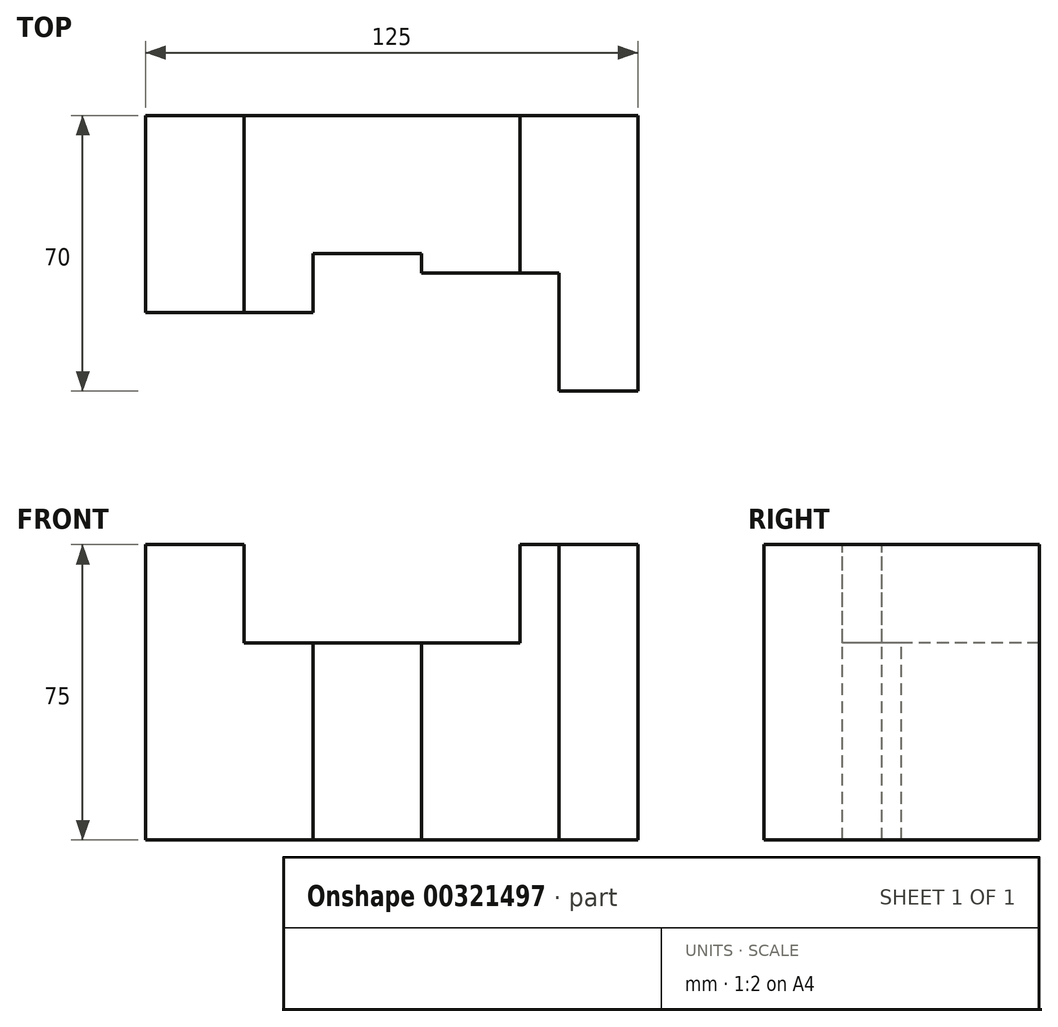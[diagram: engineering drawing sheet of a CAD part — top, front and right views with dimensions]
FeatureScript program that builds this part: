
annotation { "Feature Type Name" : "Feature", "Feature Type Description" : "" }
export const myFeature = defineFeature(function(context is Context, id is Id, definition is map)
    precondition{}
    {
        {
            var Q0;
            Q0=qCreatedBy(makeId("Right.planeOp"),FACE);
            var sketch = newSketch(context, id + "F0", { "sketchPlane" : qUnion([Q0])});
            skLineSegment(sketch, "E0.bottom", {"start": v(0, 0) * mm, "end": v(-50, 0) * mm});
            skLineSegment(sketch, "E0.top", {"start": v(0, 75) * mm, "end": v(-50, 75) * mm});
            skLineSegment(sketch, "E0.left", {"start": v(0, 0) * mm, "end": v(0, 75) * mm});
            skLineSegment(sketch, "E0.right", {"start": v(-50, 0) * mm, "end": v(-50, 75) * mm});
            skSolve(sketch);
        }
        {
            var Q0;
            Q0 = qSketchRegion(id + "F0", true);
            extrude(context, id + "F1", {"entities" : qUnion([Q0]), "depth" : 25 * mm});
        }
        {
            var Q0;
            Q0=makeQuery(id+"F1.opExtrude","CAP_FACE",FACE,{"disambiguationData":[OSD([sQuery(id+"F0.wireOp",EDGE,"E0.bottom"),sQuery(id+"F0.wireOp",EDGE,"E0.top"),sQuery(id+"F0.wireOp",EDGE,"E0.left"),sQuery(id+"F0.wireOp",EDGE,"E0.right")])],"isStart":false});
            var sketch = newSketch(context, id + "F2", { "sketchPlane" : qUnion([Q0])});
            skLineSegment(sketch, "E1.bottom", {"start": v(0, 0) * mm, "end": v(-50, 0) * mm});
            skLineSegment(sketch, "E1.top", {"start": v(0, 50) * mm, "end": v(-50, 50) * mm});
            skLineSegment(sketch, "E1.left", {"start": v(0, 0) * mm, "end": v(0, 50) * mm});
            skLineSegment(sketch, "E1.right", {"start": v(-50, 0) * mm, "end": v(-50, 50) * mm});
            skSolve(sketch);
        }
        {
            var Q0;
            Q0=makeQuery(id+"F2.imprint","IMPRINT",FACE,{"disambiguationData":[TD([[makeQuery(id+"F2.imprint","IMPRINT",EDGE,{"derivedFrom":sQuery(id+"F2.wireOp",EDGE,"E1.bottom")}),-1.0]])]});
            extrude(context, id + "F3", {"entities" : qUnion([Q0]), "operationType" : NewBodyOperationType.ADD, "depth" : 17.5 * mm});
        }
        {
            var Q0;
            Q0=makeQuery(id+"F3.opExtrude","CAP_FACE",FACE,{"disambiguationData":[OSD([sQuery(id+"F2.wireOp",EDGE,"E1.bottom"),sQuery(id+"F2.wireOp",EDGE,"E1.top"),sQuery(id+"F2.wireOp",EDGE,"E1.left"),sQuery(id+"F2.wireOp",EDGE,"E1.right")])],"isStart":false});
            var sketch = newSketch(context, id + "F4", { "sketchPlane" : qUnion([Q0])});
            skLineSegment(sketch, "E2.bottom", {"start": v(0, 0) * mm, "end": v(-35, 0) * mm});
            skLineSegment(sketch, "E2.top", {"start": v(0, 50) * mm, "end": v(-35, 50) * mm});
            skLineSegment(sketch, "E2.left", {"start": v(0, 0) * mm, "end": v(0, 50) * mm});
            skLineSegment(sketch, "E2.right", {"start": v(-35, 0) * mm, "end": v(-35, 50) * mm});
            skSolve(sketch);
        }
        {
            var Q0;
            Q0 = qSketchRegion(id + "F4", true);
            extrude(context, id + "F5", {"entities" : qUnion([Q0]), "operationType" : NewBodyOperationType.ADD, "depth" : 27.5 * mm});
        }
        {
            var Q0;
            Q0=makeQuery(id+"F5.opExtrude","CAP_FACE",FACE,{"disambiguationData":[OSD([sQuery(id+"F4.wireOp",EDGE,"E2.bottom"),sQuery(id+"F4.wireOp",EDGE,"E2.top"),sQuery(id+"F4.wireOp",EDGE,"E2.left"),sQuery(id+"F4.wireOp",EDGE,"E2.right")])],"isStart":false});
            var sketch = newSketch(context, id + "F6", { "sketchPlane" : qUnion([Q0])});
            skLineSegment(sketch, "E3.bottom", {"start": v(0, 0) * mm, "end": v(-40, 0) * mm});
            skLineSegment(sketch, "E3.top", {"start": v(0, 50) * mm, "end": v(-40, 50) * mm});
            skLineSegment(sketch, "E3.left", {"start": v(0, 0) * mm, "end": v(0, 50) * mm});
            skLineSegment(sketch, "E3.right", {"start": v(-40, 0) * mm, "end": v(-40, 50) * mm});
            skSolve(sketch);
        }
        {
            var Q0;
            Q0 = qSketchRegion(id + "F6", true);
            extrude(context, id + "F7", {"entities" : qUnion([Q0]), "operationType" : NewBodyOperationType.ADD, "depth" : 25 * mm});
        }
        {
            var Q0;
            Q0=makeQuery(id+"F7.opExtrude","CAP_FACE",FACE,{"disambiguationData":[OSD([sQuery(id+"F6.wireOp",EDGE,"E3.bottom"),sQuery(id+"F6.wireOp",EDGE,"E3.top"),sQuery(id+"F6.wireOp",EDGE,"E3.left"),sQuery(id+"F6.wireOp",EDGE,"E3.right")])],"isStart":false});
            var sketch = newSketch(context, id + "F8", { "sketchPlane" : qUnion([Q0])});
            skLineSegment(sketch, "E4.bottom", {"start": v(0, 0) * mm, "end": v(-40, 0) * mm});
            skLineSegment(sketch, "E4.top", {"start": v(0, 75) * mm, "end": v(-40, 75) * mm});
            skLineSegment(sketch, "E4.left", {"start": v(0, 0) * mm, "end": v(0, 75) * mm});
            skLineSegment(sketch, "E4.right", {"start": v(-40, 0) * mm, "end": v(-40, 75) * mm});
            skSolve(sketch);
        }
        {
            var Q0;
            Q0 = qSketchRegion(id + "F8", true);
            extrude(context, id + "F9", {"entities" : qUnion([Q0]), "operationType" : NewBodyOperationType.ADD, "depth" : 10 * mm});
        }
        {
            var Q0;
            Q0=makeQuery(id+"F9.opExtrude","CAP_FACE",FACE,{"disambiguationData":[OSD([sQuery(id+"F8.wireOp",EDGE,"E4.bottom"),sQuery(id+"F8.wireOp",EDGE,"E4.top"),sQuery(id+"F8.wireOp",EDGE,"E4.left"),sQuery(id+"F8.wireOp",EDGE,"E4.right")])],"isStart":false});
            var sketch = newSketch(context, id + "F10", { "sketchPlane" : qUnion([Q0])});
            skLineSegment(sketch, "E5.bottom", {"start": v(0, 0) * mm, "end": v(-70, 0) * mm});
            skLineSegment(sketch, "E5.top", {"start": v(0, 75) * mm, "end": v(-70, 75) * mm});
            skLineSegment(sketch, "E5.left", {"start": v(0, 0) * mm, "end": v(0, 75) * mm});
            skLineSegment(sketch, "E5.right", {"start": v(-70, 0) * mm, "end": v(-70, 75) * mm});
            skSolve(sketch);
        }
        {
            var Q0;
            Q0 = qSketchRegion(id + "F10", true);
            extrude(context, id + "F11", {"entities" : qUnion([Q0]), "operationType" : NewBodyOperationType.ADD, "depth" : 20 * mm});
        }
    });
